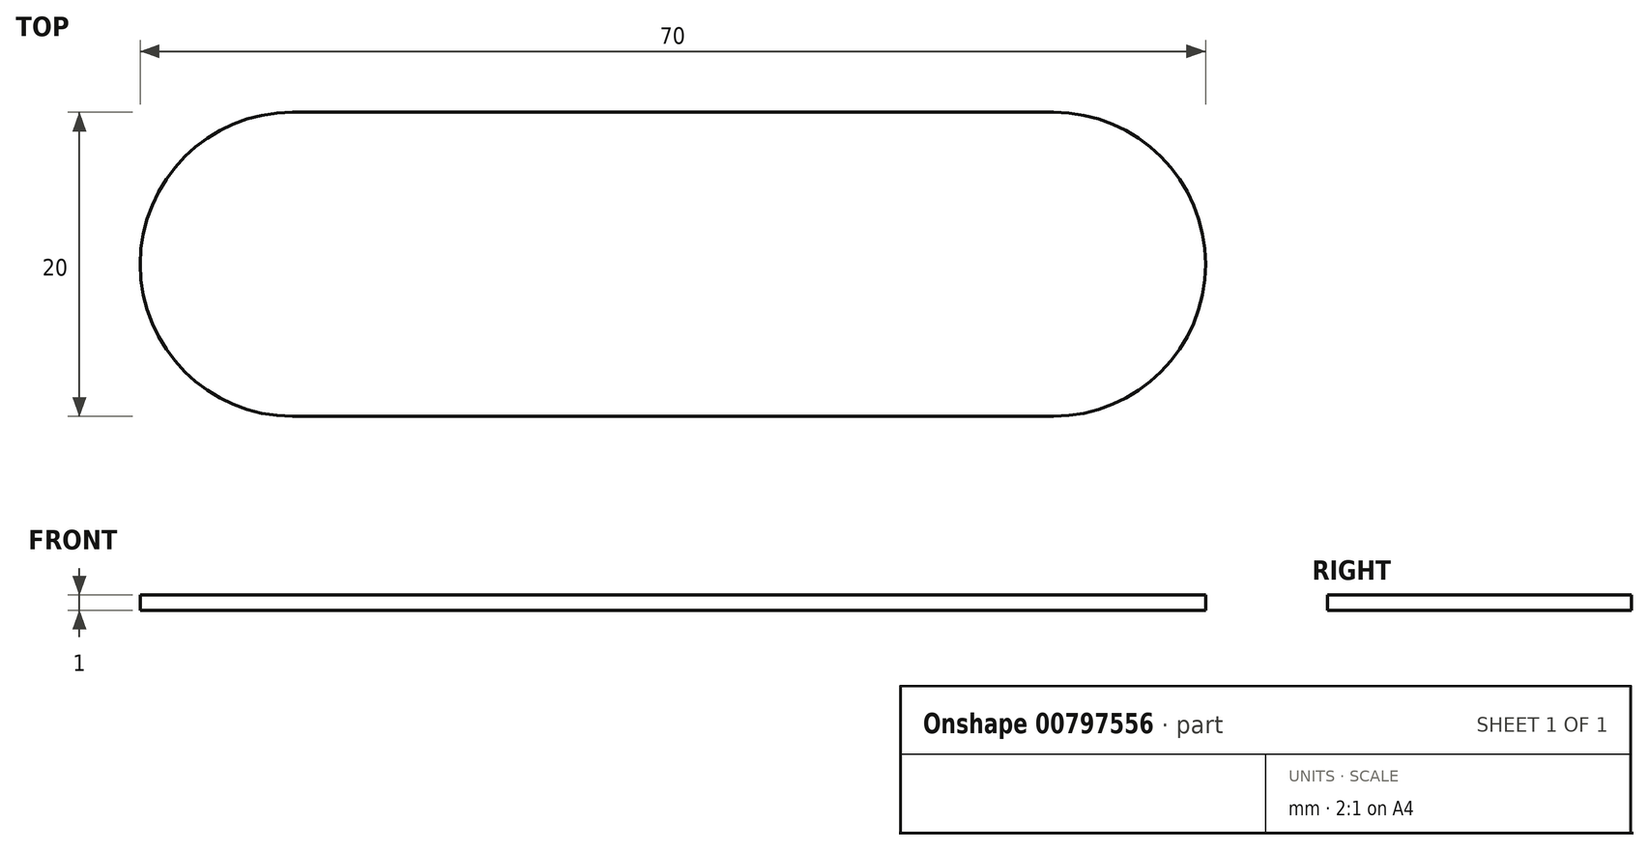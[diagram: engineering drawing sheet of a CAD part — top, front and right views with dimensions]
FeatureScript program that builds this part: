
annotation { "Feature Type Name" : "Feature", "Feature Type Description" : "" }
export const myFeature = defineFeature(function(context is Context, id is Id, definition is map)
    precondition{}
    {
        {
            var Q0;
            Q0=qCreatedBy(makeId("Top.planeOp"),FACE);
            var sketch = newSketch(context, id + "F0", { "sketchPlane" : qUnion([Q0])});
            skArc(sketch, "E0", {"start": v(0, 10) * mm, "mid": v(-10, 0) * mm, "end": v(0, -10) * mm});
            skArc(sketch, "E1", {"start": v(50, -10) * mm, "mid": v(60, 0) * mm, "end": v(50, 10) * mm});
            skLineSegment(sketch, "E2", {"start": v(0, 10) * mm, "end": v(50, 10) * mm});
            skLineSegment(sketch, "E3", {"start": v(50, -10) * mm, "end": v(0, -10) * mm});
            skSolve(sketch);
        }
        {
            var Q0;
            Q0 = qSketchRegion(id + "F0", true);
            extrude(context, id + "F1", {"entities" : qUnion([Q0]), "depth" : 1 * mm, "offsetDistance" : 25 * mm});
        }
    });
